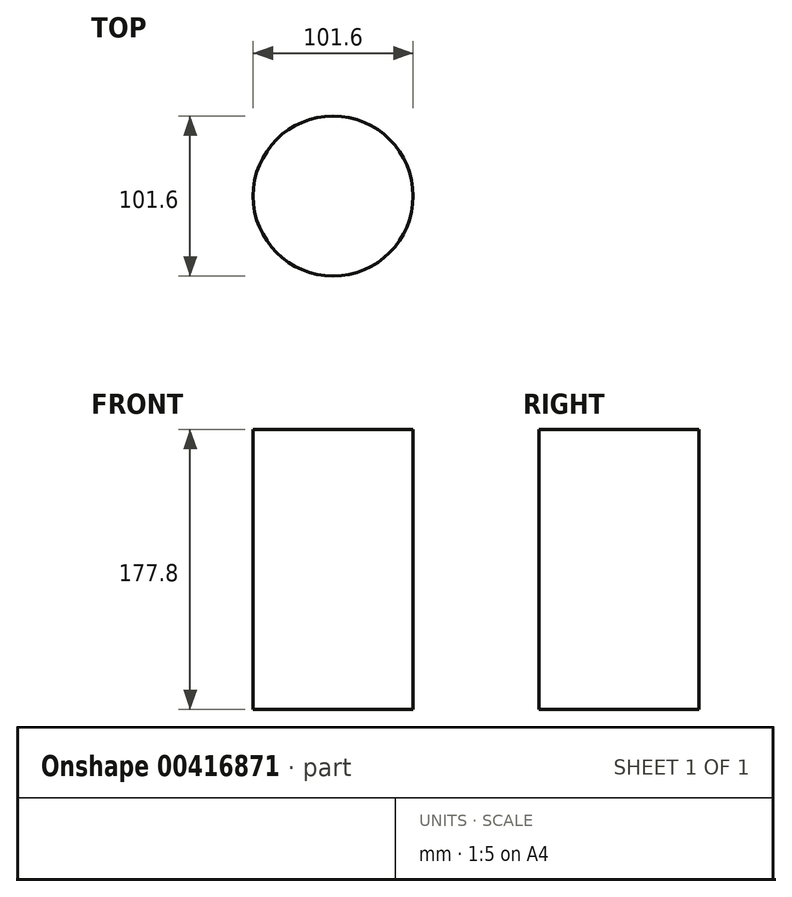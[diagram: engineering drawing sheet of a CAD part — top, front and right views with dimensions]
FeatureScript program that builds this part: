
annotation { "Feature Type Name" : "Feature", "Feature Type Description" : "" }
export const myFeature = defineFeature(function(context is Context, id is Id, definition is map)
    precondition{}
    {
        {
            var Q0;
            Q0=qCreatedBy(makeId("Top.planeOp"),FACE);
            var sketch = newSketch(context, id + "F0", { "sketchPlane" : qUnion([Q0])});
            skCircle(sketch, "E0", {"center": v(0, 0) * mm, "radius": 50.8 * mm});
            skSolve(sketch);
        }
        {
            var Q0;
            Q0 = qSketchRegion(id + "F0", true);
            extrude(context, id + "F1", {"entities" : qUnion([Q0]), "depth" : 177.8 * mm});
        }
    });
